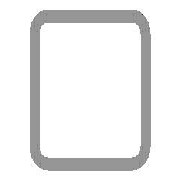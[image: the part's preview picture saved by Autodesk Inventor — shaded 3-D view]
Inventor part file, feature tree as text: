
AUTODESK INVENTOR PART (.ipt)
format: ipt  version: 2025 (Build 290162010, 162A)  size: 134,144 bytes
history: native  units: mm (DEFAULTED — no unit token found)
features: other x4, sketch x1, plane x1
ambient origin geometry x8: Origin, YZ Plane, XZ Plane, XY Plane, X Axis, Y Axis, Z Axis, Center Point
bodies: Solid1 (feature_tree), Body (feature_tree)
feature tree (6):
  parser-record x1  (decoder bookkeeping rows leaked as tree rows — omitted from the tree; the rows remain in map.json)
  other  "Driven Length"
  other  "Start Plane"
  other  "End Plane"
  sketch  "Sketch3"  dims[d3=2715.29004mm d4=0.0mm d7=8.0mm d9=60.0mm d11=60.0mm d12=4.0mm d13=-0.0mm d14=2715.29004mm d15=30.0mm d16=30.0mm d17=90.0deg d18=2715.29004mm]
  plane  "Work Plane3"
